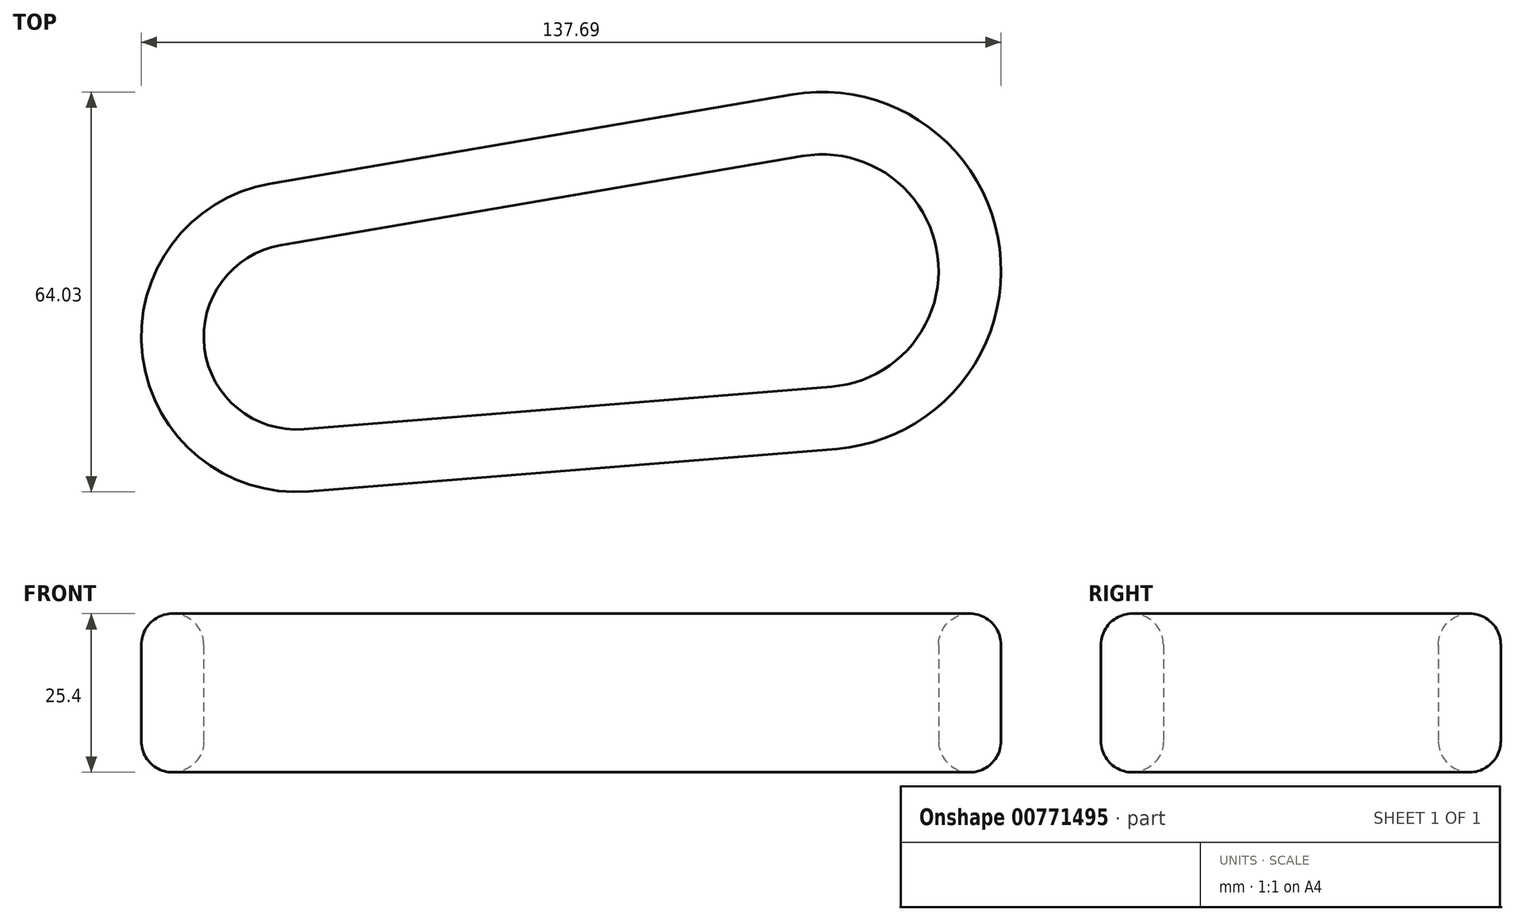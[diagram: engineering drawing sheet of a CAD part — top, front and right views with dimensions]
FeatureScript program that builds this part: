
annotation { "Feature Type Name" : "Feature", "Feature Type Description" : "" }
export const myFeature = defineFeature(function(context is Context, id is Id, definition is map)
    precondition{}
    {
        {
            var Q0;
            Q0=qCreatedBy(makeId("Top.planeOp"),FACE);
            var sketch = newSketch(context, id + "F0", { "sketchPlane" : qUnion([Q0])});
            skArc(sketch, "E0", {"start": v(-50.02, 18.75) * mm, "mid": v(-70.5, -8.84) * mm, "end": v(-43.84, -30.52) * mm});
            skArc(sketch, "E1", {"start": v(40.68, -23.7) * mm, "mid": v(66.77, 8.38) * mm, "end": v(33.56, 33.02) * mm});
            skLineSegment(sketch, "E2", {"start": v(-50.02, 18.75) * mm, "end": v(33.56, 33.02) * mm});
            skLineSegment(sketch, "E3", {"start": v(-76.58, -9.6) * mm, "end": v(79, 9.91) * mm, "construction": true});
            skLineSegment(sketch, "E4", {"start": v(-43.84, -30.52) * mm, "end": v(40.68, -23.7) * mm});
            skLineSegment(sketch, "E5.0", {"start": v(-44.64, -20.55) * mm, "end": v(39.88, -13.74) * mm});
            skArc(sketch, "E5.1", {"start": v(-48.33, 8.9) * mm, "mid": v(-60.57, -7.6) * mm, "end": v(-44.64, -20.55) * mm});
            skLineSegment(sketch, "E5.2", {"start": v(-48.33, 8.9) * mm, "end": v(35.25, 23.16) * mm});
            skArc(sketch, "E5.3", {"start": v(39.88, -13.74) * mm, "mid": v(56.85, 7.13) * mm, "end": v(35.25, 23.16) * mm});
            skSolve(sketch);
        }
        {
            var Q0;
            Q0 = qSketchRegion(id + "F0", true);
            extrude(context, id + "F1", {"entities" : qUnion([Q0]), "depth" : 25.4 * mm, "offsetDistance" : 25.4 * mm});
        }
        {
            var Q0;
            Q0=makeQuery(id+"F1.opExtrude","CAP_EDGE",EDGE,{"disambiguationData":[OSD([sQuery(id+"F0.wireOp",EDGE,"E5.0")])],"isStart":false});
            var Q1;
            Q1=makeQuery(id+"F1.opExtrude","CAP_EDGE",EDGE,{"disambiguationData":[OSD([sQuery(id+"F0.wireOp",EDGE,"E4")])],"isStart":false});
            fillet(context, id + "F2", {"entities" : qUnion([Q0, Q1]), "radius" : 5 * mm, "tangentPropagation" : true, "allowEdgeOverflow" : false});
        }
        {
            var Q0;
            Q0=makeQuery(id+"F1.opExtrude","CAP_FACE",FACE,{"disambiguationData":[OSD([sQuery(id+"F0.wireOp",EDGE,"E0"),sQuery(id+"F0.wireOp",EDGE,"E1"),sQuery(id+"F0.wireOp",EDGE,"E2"),sQuery(id+"F0.wireOp",EDGE,"E4"),sQuery(id+"F0.wireOp",EDGE,"E5.0"),sQuery(id+"F0.wireOp",EDGE,"E5.1"),sQuery(id+"F0.wireOp",EDGE,"E5.2"),sQuery(id+"F0.wireOp",EDGE,"E5.3")])],"isStart":true});
            fillet(context, id + "F3", {"entities" : qUnion([Q0]), "radius" : 5 * mm, "tangentPropagation" : true, "allowEdgeOverflow" : false});
        }
    });
